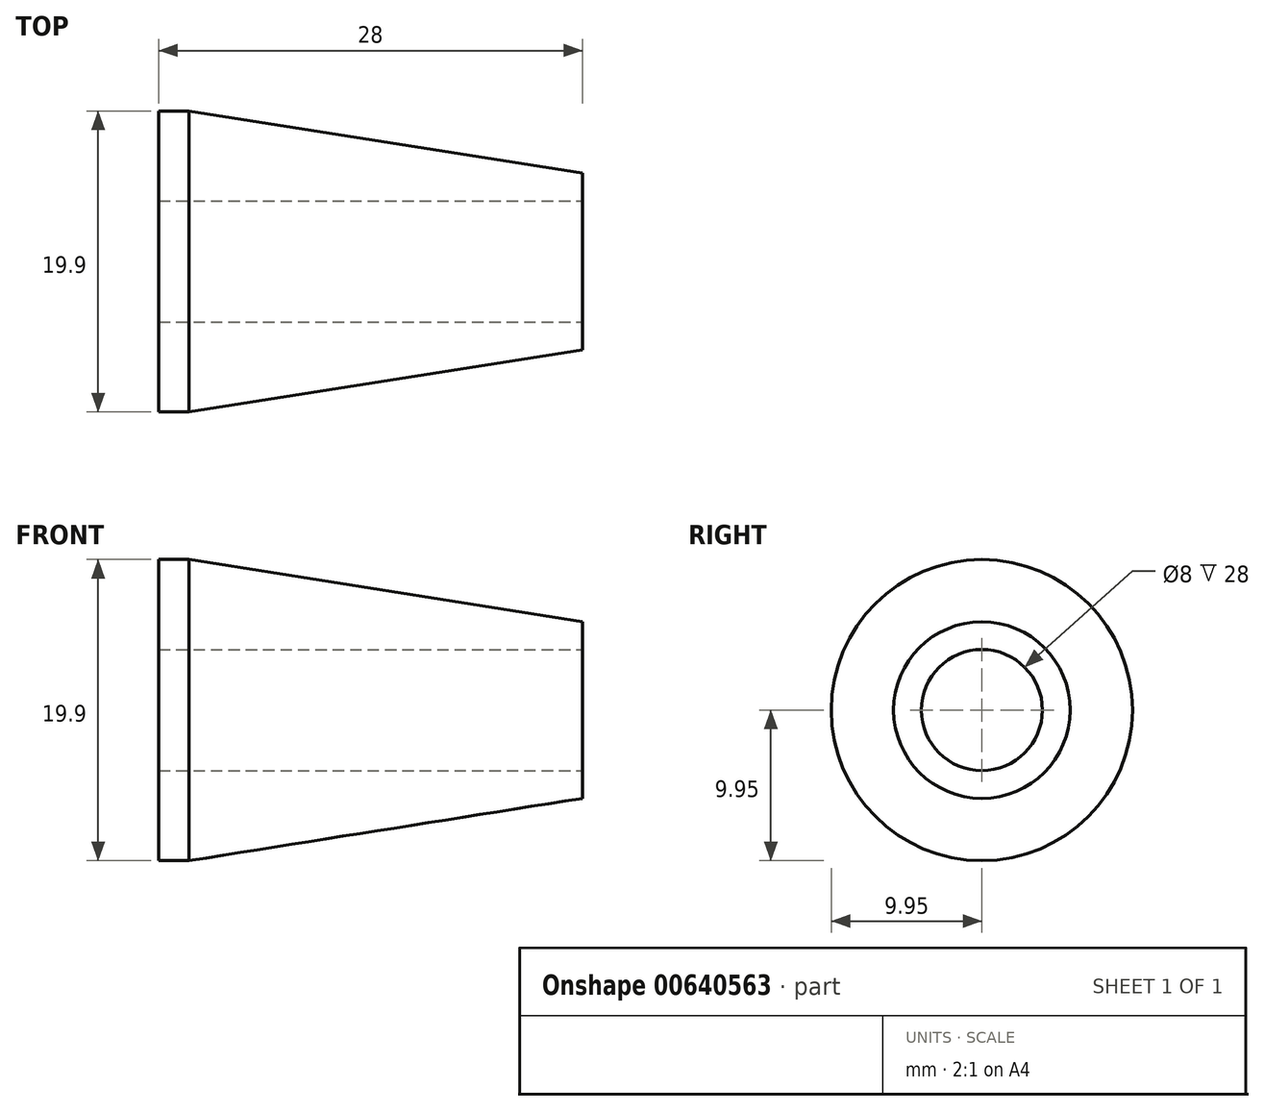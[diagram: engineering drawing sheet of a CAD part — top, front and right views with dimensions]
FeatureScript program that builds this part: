
annotation { "Feature Type Name" : "Feature", "Feature Type Description" : "" }
export const myFeature = defineFeature(function(context is Context, id is Id, definition is map)
    precondition{}
    {
        {
            var Q0;
            Q0=qCreatedBy(makeId("Front.planeOp"),FACE);
            var sketch = newSketch(context, id + "F0", { "sketchPlane" : qUnion([Q0])});
            skLineSegment(sketch, "E0", {"start": v(26, 5.83) * mm, "end": v(0, 9.95) * mm});
            skLineSegment(sketch, "E1", {"start": v(0, 4) * mm, "end": v(26, 4) * mm});
            skLineSegment(sketch, "E2", {"start": v(26, 4) * mm, "end": v(26, 5.83) * mm});
            skLineSegment(sketch, "E3", {"start": v(30.81, 0) * mm, "end": v(-11.69, 0) * mm, "construction": true});
            skLineSegment(sketch, "E4", {"start": v(0, 9.95) * mm, "end": v(0, 4) * mm, "construction": true});
            skLineSegment(sketch, "E5", {"start": v(0, 9.95) * mm, "end": v(-2, 9.95) * mm});
            skLineSegment(sketch, "E6", {"start": v(-2, 9.95) * mm, "end": v(-2, 4) * mm});
            skLineSegment(sketch, "E7", {"start": v(-2, 4) * mm, "end": v(0, 4) * mm});
            skSolve(sketch);
        }
        {
            var Q0;
            Q0 = qSketchRegion(id + "F0", true);
            var Q1;
            Q1=sQuery(id+"F0.wireOp",EDGE,"E3");
            revolve(context, id + "F1", {"entities" : qUnion([Q0]), "axis" : qUnion([Q1]), "revolveType" : RevolveType.FULL});
        }
    });
